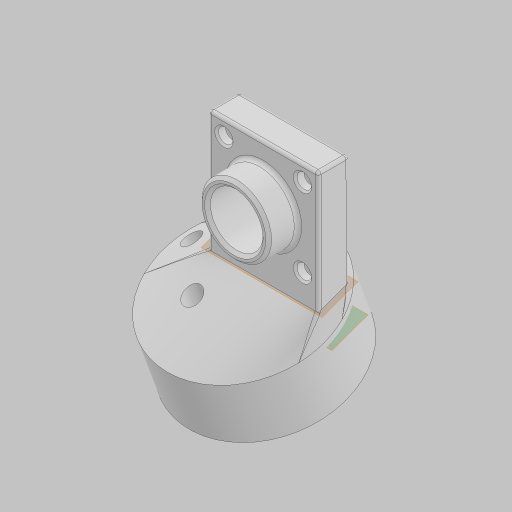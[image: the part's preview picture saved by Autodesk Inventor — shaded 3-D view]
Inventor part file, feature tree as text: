
AUTODESK INVENTOR PART (.ipt)
format: ipt  version: 2023.5 (Build 275446000, 446)  size: 451,072 bytes
history: native  units: in
note: dims shown in document units (in); Inventor stores cm internally (conversion verified against a paired STEP export)
features: extrude x7, hole x3, fillet x3, other x3, projected_geometry x3, plane x2, chamfer x2, loft x1, thicken_offset x1, sketch x1, revolve x1
ambient origin geometry x8: Origin, YZ Plane, XZ Plane, XY Plane, X Axis, Y Axis, Z Axis, Center Point
bodies: Solid1 (feature_tree)
feature tree (27):
  extrude  "Extrusion1"  Depth=0.525in
  extrude  "Extrusion2"  Depth=1.875in TaperAngle=0.0deg
  plane  "Work Plane1"
  extrude  "Extrusion3"  Depth=0.481in
  loft  "Loft1"
  extrude  "Extrusion4"  Depth=0.6in
  hole  "Hole1"  [1 undecoded]
  extrude  "Extrusion5"  Depth=0.1in TaperAngle=0.0deg
  extrude  "Extrusion6"  TaperAngle=0.0deg  [1 undecoded]
  hole  "Hole2"  [1 undecoded]
  plane  "Work Plane2"
  fillet  "Fillet1"  Radius=1.6in
  chamfer  "Chamfer1"  Distance=0.3in
  fillet  "Fillet2"  Radius=1.1875in
  extrude  "Extrusion7"  Depth=0.5in TaperAngle=0.0deg
  fillet  "Fillet3"  Radius=0.1839in
  chamfer  "Chamfer2"  Distance=1.3386in
  thicken_offset  "Thicken1"
  hole  "Hole4"  [1 undecoded]
  other  "Edges1"
  other  "Edges2"
  projected_geometry  "Projected Loop1"
  projected_geometry  "Projected Loop2"
  sketch  "Sketch11"  dims[d0=1.875in d1=0.525in d2=1.875in d3=0.0in d4=0.481in d5=1.875in d6=0.0in d7=0.6in d9=2.75in d10=0.1in d11=0.0in d12=0.0in d13=90.0deg d14=0.0in d15=90.0deg d16=1.6in d17=0.3in d18=0.0in d19=0.9in d20=0.75in d21=0.119in d22=0.25in d23=0.6871in d24=1.0in d25=0.8108in d26=1.1875in d27=0.5in d28=0.0in d29=0.1839in d30=1.3386in d31=0.15in d32=0.0in d33=0.094in d34=0.75in d35=0.251in d36=0.15in d37=0.6871in d38=1.0in d39=0.8108in d40=0.9792in d41=0.9792in d42=315.0deg d52=0.05in d53=0.05in d54=0.125in d55=45.0deg d56=0.0625in d57=1.0in d58=1.0in d59=0.0in d60=0.25in d61=0.0312in d62=0.125in d63=45.0deg d64=0.2405in d65=90.0deg d66=1.0in d67=1.0in d68=0.177in d69=0.75in d70=0.313in d71=1.45in d72=0.5635in d73=1.0in d74=0.8108in]
  other  "Srf1"
  revolve  "RevolutionSrf1"  [1 undecoded]
  projected_geometry  "Project Cut Edges1"
note: 5 required parameter values undecoded (feature->parameter linkage not recoverable at this tier; creation-order binding heuristic only, values carry confidence <= 0.55)